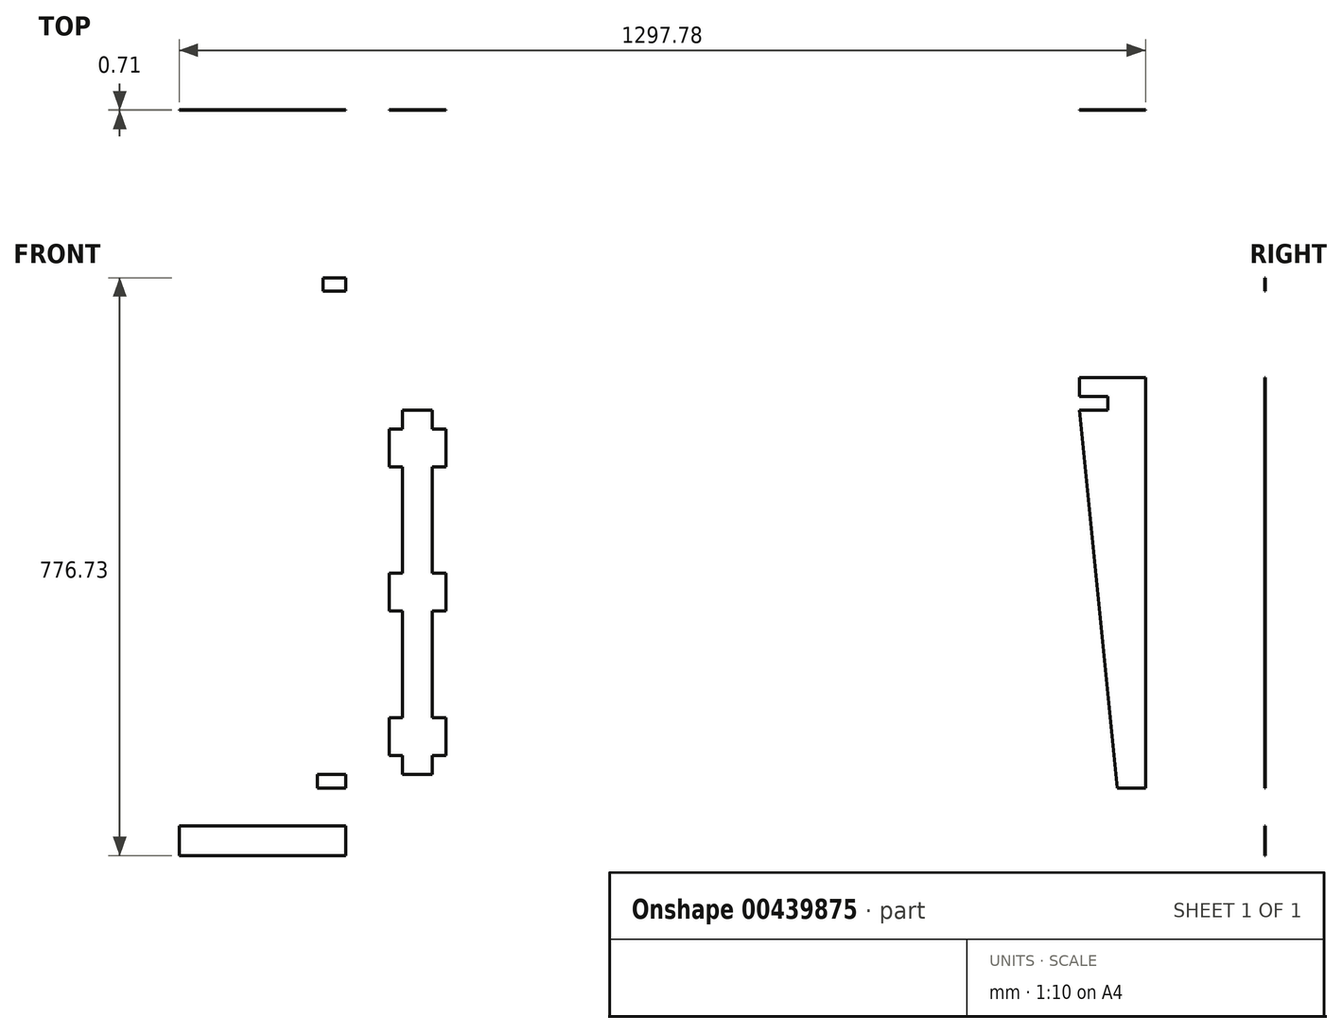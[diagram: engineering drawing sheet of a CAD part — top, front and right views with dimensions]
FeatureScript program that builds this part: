
annotation { "Feature Type Name" : "Feature", "Feature Type Description" : "" }
export const myFeature = defineFeature(function(context is Context, id is Id, definition is map)
    precondition{}
    {
        {
            assignVariable(context, id + "F0", {"name" : "ply34", "anyValue" : .71});
        }
        {
            var Q0;
            Q0=qCreatedBy(makeId("Front.planeOp"),FACE);
            var sketch = newSketch(context, id + "F1", { "sketchPlane" : qUnion([Q0])});
            skLineSegment(sketch, "E0.bottom", {"start": v(-508, 0) * mm, "end": v(508, 0) * mm});
            skLineSegment(sketch, "E0.top", {"start": v(-508, -76.2) * mm, "end": v(508, -76.2) * mm});
            skLineSegment(sketch, "E0.left", {"start": v(-508, 0) * mm, "end": v(-508, -76.2) * mm});
            skLineSegment(sketch, "E0.right", {"start": v(508, 0) * mm, "end": v(508, -76.2) * mm});
            skLineSegment(sketch, "E1.bottom", {"start": v(-152.4, -34.8) * mm, "end": v(152.4, -34.8) * mm});
            skLineSegment(sketch, "E1.top", {"start": v(-152.4, -41.4) * mm, "end": v(152.4, -41.4) * mm});
            skLineSegment(sketch, "E1.left", {"start": v(-152.4, -34.8) * mm, "end": v(-152.4, -41.4) * mm});
            skLineSegment(sketch, "E1.right", {"start": v(152.4, -34.8) * mm, "end": v(152.4, -41.4) * mm});
            skPoint(sketch, "E1.middle", {"position": v(0, -38.1) * mm});
            skPoint(sketch, "E1.middle.positionSnap0", {"position": v(508, -38.1) * mm});
            skPoint(sketch, "E1.centerSnap0", {"position": v(508, -38.1) * mm});
            skLineSegment(sketch, "E2.bottom", {"start": v(508, -29.08) * mm, "end": v(457.2, -29.08) * mm});
            skLineSegment(sketch, "E2.top", {"start": v(508, -47.12) * mm, "end": v(457.2, -47.12) * mm});
            skLineSegment(sketch, "E2.left", {"start": v(508, -29.08) * mm, "end": v(508, -47.12) * mm});
            skLineSegment(sketch, "E2.right", {"start": v(457.2, -29.08) * mm, "end": v(457.2, -47.12) * mm});
            skPoint(sketch, "E2.middle", {"position": v(482.6, -38.1) * mm});
            skLineSegment(sketch, "E3.bottom", {"start": v(-508, 0) * mm, "end": v(-477.27, 0) * mm});
            skLineSegment(sketch, "E3.top", {"start": v(-508, -18.03) * mm, "end": v(-477.27, -18.03) * mm});
            skLineSegment(sketch, "E3.left", {"start": v(-508, 0) * mm, "end": v(-508, -18.03) * mm});
            skLineSegment(sketch, "E3.right", {"start": v(-477.27, 0) * mm, "end": v(-477.27, -18.03) * mm});
            skLineSegment(sketch, "E4.bottom", {"start": v(-508, -76.2) * mm, "end": v(-477.27, -76.2) * mm});
            skLineSegment(sketch, "E4.top", {"start": v(-508, -58.17) * mm, "end": v(-477.27, -58.17) * mm});
            skLineSegment(sketch, "E4.left", {"start": v(-508, -76.2) * mm, "end": v(-508, -58.17) * mm});
            skLineSegment(sketch, "E4.right", {"start": v(-477.27, -76.2) * mm, "end": v(-477.27, -58.17) * mm});
            skLineSegment(sketch, "E5", {"start": v(-477.27, -177.8) * mm, "end": v(-477.27, -685.8) * mm});
            skLineSegment(sketch, "E6", {"start": v(-553.47, -134.37) * mm, "end": v(-705.87, -685.8) * mm});
            skLineSegment(sketch, "E7", {"start": v(-705.87, -685.8) * mm, "end": v(-477.27, -685.8) * mm});
            skLineSegment(sketch, "E8", {"start": v(-508, -177.8) * mm, "end": v(-508, -159.77) * mm});
            skLineSegment(sketch, "E9", {"start": v(-508, -159.77) * mm, "end": v(-477.27, -159.77) * mm});
            skLineSegment(sketch, "E10", {"start": v(-477.27, -159.77) * mm, "end": v(-477.27, -134.37) * mm});
            skLineSegment(sketch, "E11", {"start": v(-477.27, -134.37) * mm, "end": v(-553.47, -134.37) * mm});
            skLineSegment(sketch, "E12", {"start": v(-508, -177.8) * mm, "end": v(-477.27, -177.8) * mm});
            skLineSegment(sketch, "E13.bottom", {"start": v(-508, -159.77) * mm, "end": v(-520.7, -159.77) * mm, "construction": true});
            skLineSegment(sketch, "E13.top", {"start": v(-508, -177.8) * mm, "end": v(-520.7, -177.8) * mm, "construction": true});
            skLineSegment(sketch, "E13.left", {"start": v(-508, -159.77) * mm, "end": v(-508, -177.8) * mm, "construction": true});
            skLineSegment(sketch, "E13.right", {"start": v(-520.7, -159.77) * mm, "end": v(-520.7, -177.8) * mm, "construction": true});
            skLineSegment(sketch, "E14.bottom", {"start": v(-520.7, -159.77) * mm, "end": v(-538.73, -159.77) * mm, "construction": true});
            skLineSegment(sketch, "E14.top", {"start": v(-520.7, -685.8) * mm, "end": v(-538.73, -685.8) * mm, "construction": true});
            skLineSegment(sketch, "E14.left", {"start": v(-520.7, -159.77) * mm, "end": v(-520.7, -685.8) * mm, "construction": true});
            skLineSegment(sketch, "E14.right", {"start": v(-538.73, -159.77) * mm, "end": v(-538.73, -685.8) * mm, "construction": true});
            skLineSegment(sketch, "E15.bottom", {"start": v(-538.73, -203.2) * mm, "end": v(-520.7, -203.2) * mm});
            skLineSegment(sketch, "E15.top", {"start": v(-538.73, -254) * mm, "end": v(-520.7, -254) * mm});
            skLineSegment(sketch, "E15.left", {"start": v(-538.73, -203.2) * mm, "end": v(-538.73, -254) * mm});
            skLineSegment(sketch, "E15.right", {"start": v(-520.7, -203.2) * mm, "end": v(-520.7, -254) * mm});
            skLineSegment(sketch, "E16.bottom", {"start": v(-538.73, -397.38) * mm, "end": v(-520.7, -397.38) * mm});
            skLineSegment(sketch, "E16.top", {"start": v(-538.73, -448.18) * mm, "end": v(-520.7, -448.18) * mm});
            skLineSegment(sketch, "E16.left", {"start": v(-538.73, -397.38) * mm, "end": v(-538.73, -448.18) * mm});
            skLineSegment(sketch, "E16.right", {"start": v(-520.7, -397.38) * mm, "end": v(-520.7, -448.18) * mm});
            skPoint(sketch, "E17", {"position": v(-520.7, -422.78) * mm});
            skLineSegment(sketch, "E18.bottom", {"start": v(-665.73, -685.8) * mm, "end": v(-627.63, -685.8) * mm});
            skLineSegment(sketch, "E18.top", {"start": v(-665.73, -667.77) * mm, "end": v(-627.63, -667.77) * mm});
            skLineSegment(sketch, "E18.left", {"start": v(-665.73, -685.8) * mm, "end": v(-665.73, -667.77) * mm});
            skLineSegment(sketch, "E18.right", {"start": v(-627.63, -685.8) * mm, "end": v(-627.63, -667.77) * mm});
            skPoint(sketch, "E19.oppositeSnap0", {"position": v(-646.68, -667.77) * mm});
            skLineSegment(sketch, "E19.bottom", {"start": v(-477.27, -685.8) * mm, "end": v(-515.37, -685.8) * mm});
            skLineSegment(sketch, "E19.top", {"start": v(-477.27, -667.77) * mm, "end": v(-515.37, -667.77) * mm});
            skLineSegment(sketch, "E19.left", {"start": v(-477.27, -685.8) * mm, "end": v(-477.27, -667.77) * mm});
            skLineSegment(sketch, "E19.right", {"start": v(-515.37, -685.8) * mm, "end": v(-515.37, -667.77) * mm});
            skLineSegment(sketch, "E20.bottom", {"start": v(-538.73, -642.37) * mm, "end": v(-520.7, -642.37) * mm});
            skLineSegment(sketch, "E20.top", {"start": v(-538.73, -591.57) * mm, "end": v(-520.7, -591.57) * mm});
            skLineSegment(sketch, "E20.left", {"start": v(-538.73, -642.37) * mm, "end": v(-538.73, -591.57) * mm});
            skLineSegment(sketch, "E20.right", {"start": v(-520.7, -642.37) * mm, "end": v(-520.7, -591.57) * mm});
            skPoint(sketch, "E21.firstSnap0", {"position": v(-514.35, -159.77) * mm});
            skLineSegment(sketch, "E21.bottom", {"start": v(-401.07, -159.77) * mm, "end": v(-360.93, -159.77) * mm});
            skLineSegment(sketch, "E21.top", {"start": v(-401.07, -667.77) * mm, "end": v(-360.93, -667.77) * mm});
            skLineSegment(sketch, "E21.left", {"start": v(-401.07, -159.77) * mm, "end": v(-401.07, -667.77) * mm});
            skLineSegment(sketch, "E21.right", {"start": v(-360.93, -159.77) * mm, "end": v(-360.93, -667.77) * mm});
            skLineSegment(sketch, "E22.bottom", {"start": v(-401.07, -203.2) * mm, "end": v(-419.1, -203.2) * mm});
            skLineSegment(sketch, "E22.top", {"start": v(-401.07, -254) * mm, "end": v(-419.1, -254) * mm});
            skLineSegment(sketch, "E22.left", {"start": v(-401.07, -203.2) * mm, "end": v(-401.07, -254) * mm});
            skLineSegment(sketch, "E22.right", {"start": v(-419.1, -203.2) * mm, "end": v(-419.1, -254) * mm});
            skLineSegment(sketch, "E23.bottom", {"start": v(-360.93, -254) * mm, "end": v(-342.9, -254) * mm});
            skLineSegment(sketch, "E23.top", {"start": v(-360.93, -203.2) * mm, "end": v(-342.9, -203.2) * mm});
            skLineSegment(sketch, "E23.left", {"start": v(-360.93, -254) * mm, "end": v(-360.93, -203.2) * mm});
            skLineSegment(sketch, "E23.right", {"start": v(-342.9, -254) * mm, "end": v(-342.9, -203.2) * mm});
            skLineSegment(sketch, "E24.bottom", {"start": v(-401.07, -397.38) * mm, "end": v(-419.1, -397.38) * mm});
            skLineSegment(sketch, "E24.top", {"start": v(-401.07, -448.18) * mm, "end": v(-419.1, -448.18) * mm});
            skLineSegment(sketch, "E24.left", {"start": v(-401.07, -397.38) * mm, "end": v(-401.07, -448.18) * mm});
            skLineSegment(sketch, "E24.right", {"start": v(-419.1, -397.38) * mm, "end": v(-419.1, -448.18) * mm});
            skLineSegment(sketch, "E25.bottom", {"start": v(-401.07, -642.37) * mm, "end": v(-419.1, -642.37) * mm});
            skLineSegment(sketch, "E25.top", {"start": v(-401.07, -591.57) * mm, "end": v(-419.1, -591.57) * mm});
            skLineSegment(sketch, "E25.left", {"start": v(-401.07, -642.37) * mm, "end": v(-401.07, -591.57) * mm});
            skLineSegment(sketch, "E25.right", {"start": v(-419.1, -642.37) * mm, "end": v(-419.1, -591.57) * mm});
            skLineSegment(sketch, "E26.bottom", {"start": v(-360.93, -642.37) * mm, "end": v(-342.9, -642.37) * mm});
            skLineSegment(sketch, "E26.top", {"start": v(-360.93, -591.57) * mm, "end": v(-342.9, -591.57) * mm});
            skLineSegment(sketch, "E26.left", {"start": v(-360.93, -642.37) * mm, "end": v(-360.93, -591.57) * mm});
            skLineSegment(sketch, "E26.right", {"start": v(-342.9, -642.37) * mm, "end": v(-342.9, -591.57) * mm});
            skLineSegment(sketch, "E27.bottom", {"start": v(-360.93, -448.18) * mm, "end": v(-342.9, -448.18) * mm});
            skLineSegment(sketch, "E27.top", {"start": v(-360.93, -397.38) * mm, "end": v(-342.9, -397.38) * mm});
            skLineSegment(sketch, "E27.left", {"start": v(-360.93, -448.18) * mm, "end": v(-360.93, -397.38) * mm});
            skLineSegment(sketch, "E27.right", {"start": v(-342.9, -448.18) * mm, "end": v(-342.9, -397.38) * mm});
            skLineSegment(sketch, "E28", {"start": v(-665.73, -667.77) * mm, "end": v(-700.88, -667.77) * mm, "construction": true});
            skLineSegment(sketch, "E29.bottom", {"start": v(-700.88, -736.6) * mm, "end": v(-477.27, -736.6) * mm});
            skLineSegment(sketch, "E29.top", {"start": v(-700.88, -776.73) * mm, "end": v(-477.27, -776.73) * mm});
            skLineSegment(sketch, "E29.left", {"start": v(-700.88, -736.6) * mm, "end": v(-700.88, -776.73) * mm});
            skLineSegment(sketch, "E29.right", {"start": v(-477.27, -736.6) * mm, "end": v(-477.27, -776.73) * mm});
            skLineSegment(sketch, "E30.bottom", {"start": v(-627.63, -736.6) * mm, "end": v(-665.73, -736.6) * mm});
            skLineSegment(sketch, "E30.top", {"start": v(-627.63, -718.57) * mm, "end": v(-665.73, -718.57) * mm});
            skLineSegment(sketch, "E30.left", {"start": v(-627.63, -736.6) * mm, "end": v(-627.63, -718.57) * mm});
            skLineSegment(sketch, "E30.right", {"start": v(-665.73, -736.6) * mm, "end": v(-665.73, -718.57) * mm});
            skLineSegment(sketch, "E31.bottom", {"start": v(-477.27, -736.6) * mm, "end": v(-515.37, -736.6) * mm});
            skLineSegment(sketch, "E31.top", {"start": v(-477.27, -718.57) * mm, "end": v(-515.37, -718.57) * mm});
            skLineSegment(sketch, "E31.left", {"start": v(-477.27, -736.6) * mm, "end": v(-477.27, -718.57) * mm});
            skLineSegment(sketch, "E31.right", {"start": v(-515.37, -736.6) * mm, "end": v(-515.37, -718.57) * mm});
            skLineSegment(sketch, "E32.bottom", {"start": v(-627.63, -776.73) * mm, "end": v(-665.73, -776.73) * mm});
            skLineSegment(sketch, "E32.top", {"start": v(-627.63, -794.77) * mm, "end": v(-665.73, -794.77) * mm});
            skLineSegment(sketch, "E32.left", {"start": v(-627.63, -776.73) * mm, "end": v(-627.63, -794.77) * mm});
            skLineSegment(sketch, "E32.right", {"start": v(-665.73, -776.73) * mm, "end": v(-665.73, -794.77) * mm});
            skLineSegment(sketch, "E33.bottom", {"start": v(-477.27, -776.73) * mm, "end": v(-515.37, -776.73) * mm});
            skLineSegment(sketch, "E33.top", {"start": v(-477.27, -794.77) * mm, "end": v(-515.37, -794.77) * mm});
            skLineSegment(sketch, "E33.left", {"start": v(-477.27, -776.73) * mm, "end": v(-477.27, -794.77) * mm});
            skLineSegment(sketch, "E33.right", {"start": v(-515.37, -776.73) * mm, "end": v(-515.37, -794.77) * mm});
            skLineSegment(sketch, "E34.bottom", {"start": v(596.9, -685.8) * mm, "end": v(558.8, -685.8) * mm, "construction": true});
            skLineSegment(sketch, "E34.top", {"start": v(596.9, -134.37) * mm, "end": v(558.8, -134.37) * mm, "construction": true});
            skLineSegment(sketch, "E34.left", {"start": v(596.9, -685.8) * mm, "end": v(596.9, -134.37) * mm, "construction": true});
            skLineSegment(sketch, "E34.right", {"start": v(558.8, -685.8) * mm, "end": v(558.8, -134.37) * mm, "construction": true});
            skLineSegment(sketch, "E35", {"start": v(596.9, -134.37) * mm, "end": v(508, -134.37) * mm});
            skLineSegment(sketch, "E36", {"start": v(508, -134.37) * mm, "end": v(508, -159.77) * mm});
            skLineSegment(sketch, "E37", {"start": v(508, -159.77) * mm, "end": v(546.1, -159.77) * mm});
            skLineSegment(sketch, "E38", {"start": v(546.1, -159.77) * mm, "end": v(546.1, -177.8) * mm});
            skLineSegment(sketch, "E39", {"start": v(546.1, -177.8) * mm, "end": v(508, -177.8) * mm});
            skLineSegment(sketch, "E40", {"start": v(508, -177.8) * mm, "end": v(558.8, -685.8) * mm});
            skLineSegment(sketch, "E41", {"start": v(596.9, -685.8) * mm, "end": v(558.8, -685.8) * mm});
            skLineSegment(sketch, "E42", {"start": v(596.9, -685.8) * mm, "end": v(596.9, -134.37) * mm});
            skLineSegment(sketch, "E43", {"start": v(-401.07, -177.8) * mm, "end": v(-360.93, -177.8) * mm});
            skSolve(sketch);
        }
        {
            var Q0;
            {var subQ5=sQuery(id+"F1.wireOp",EDGE,"E0.bottom");Q0=makeQuery(id+"F1.imprint","IMPRINT",FACE,{"disambiguationData":[TD([[makeQuery(id+"F1.imprint","IMPRINT",EDGE,{"derivedFrom":subQ5}),-1.0]])]});}
            var Q1;
            Q1=makeQuery(id+"F1.imprint","IMPRINT",FACE,{"disambiguationData":[TD([[makeQuery(id+"F1.imprint","IMPRINT",EDGE,{"derivedFrom":sQuery(id+"F1.wireOp",EDGE,"E35")}),1.0]])]});
            var Q2;
            Q2=makeQuery(id+"F1.imprint","IMPRINT",FACE,{"disambiguationData":[TD([[makeQuery(id+"F1.imprint","IMPRINT",EDGE,{"derivedFrom":sQuery(id+"F1.wireOp",EDGE,"E5")}),-1.0]])]});
            var Q3;
            Q3=makeQuery(id+"F1.imprint","IMPRINT",FACE,{"disambiguationData":[TD([[makeQuery(id+"F1.imprint","IMPRINT",EDGE,{"derivedFrom":sQuery(id+"F1.wireOp",EDGE,"E22.bottom")}),1.0]])]});
            var Q4;
            Q4=makeQuery(id+"F1.imprint","IMPRINT",FACE,{"disambiguationData":[TD([[makeQuery(id+"F1.imprint","IMPRINT",EDGE,{"derivedFrom":sQuery(id+"F1.wireOp",EDGE,"E23.bottom")}),1.0]])]});
            var Q5;
            Q5=makeQuery(id+"F1.imprint","IMPRINT",FACE,{"disambiguationData":[TD([[makeQuery(id+"F1.imprint","IMPRINT",EDGE,{"derivedFrom":sQuery(id+"F1.wireOp",EDGE,"E27.bottom")}),1.0]])]});
            var Q6;
            Q6=makeQuery(id+"F1.imprint","IMPRINT",FACE,{"disambiguationData":[TD([[makeQuery(id+"F1.imprint","IMPRINT",EDGE,{"derivedFrom":sQuery(id+"F1.wireOp",EDGE,"E24.bottom")}),1.0]])]});
            var Q7;
            Q7=makeQuery(id+"F1.imprint","IMPRINT",FACE,{"disambiguationData":[TD([[makeQuery(id+"F1.imprint","IMPRINT",EDGE,{"derivedFrom":sQuery(id+"F1.wireOp",EDGE,"E25.bottom")}),-1.0]])]});
            var Q8;
            Q8=makeQuery(id+"F1.imprint","IMPRINT",FACE,{"disambiguationData":[TD([[makeQuery(id+"F1.imprint","IMPRINT",EDGE,{"derivedFrom":sQuery(id+"F1.wireOp",EDGE,"E26.bottom")}),1.0]])]});
            var Q9;
            Q9=makeQuery(id+"F1.imprint","IMPRINT",FACE,{"disambiguationData":[TD([[makeQuery(id+"F1.imprint","IMPRINT",EDGE,{"derivedFrom":sQuery(id+"F1.wireOp",EDGE,"E31.bottom")}),-1.0]])]});
            var Q10;
            {var subQ3=sQuery(id+"F1.wireOp",EDGE,"E29.left");Q10=makeQuery(id+"F1.imprint","IMPRINT",FACE,{"disambiguationData":[TD([[makeQuery(id+"F1.imprint","IMPRINT",EDGE,{"derivedFrom":subQ3}),1.0]])]});}
            var Q11;
            Q11=makeQuery(id+"F1.imprint","IMPRINT",FACE,{"disambiguationData":[TD([[makeQuery(id+"F1.imprint","IMPRINT",EDGE,{"derivedFrom":sQuery(id+"F1.wireOp",EDGE,"E33.bottom")}),1.0]])]});
            var Q12;
            Q12=makeQuery(id+"F1.imprint","IMPRINT",FACE,{"disambiguationData":[TD([[makeQuery(id+"F1.imprint","IMPRINT",EDGE,{"derivedFrom":sQuery(id+"F1.wireOp",EDGE,"E30.bottom")}),-1.0]])]});
            var Q13;
            Q13=makeQuery(id+"F1.imprint","IMPRINT",FACE,{"disambiguationData":[TD([[makeQuery(id+"F1.imprint","IMPRINT",EDGE,{"derivedFrom":sQuery(id+"F1.wireOp",EDGE,"E32.bottom")}),1.0]])]});
            var Q14;
            {var subQ1=sQuery(id+"F1.wireOp",EDGE,"E21.top");Q14=makeQuery(id+"F1.imprint","IMPRINT",FACE,{"disambiguationData":[TD([[makeQuery(id+"F1.imprint","IMPRINT",EDGE,{"derivedFrom":subQ1}),1.0]])]});}
            extrude(context, id + "F2", {"entities" : qUnion([Q0, Q1, Q2, Q3, Q4, Q5, Q6, Q7, Q8, Q9, Q10, Q11, Q12, Q13, Q14]), "depth" : (getVariable(context, 'ply34')) * mm});
        }
    });
